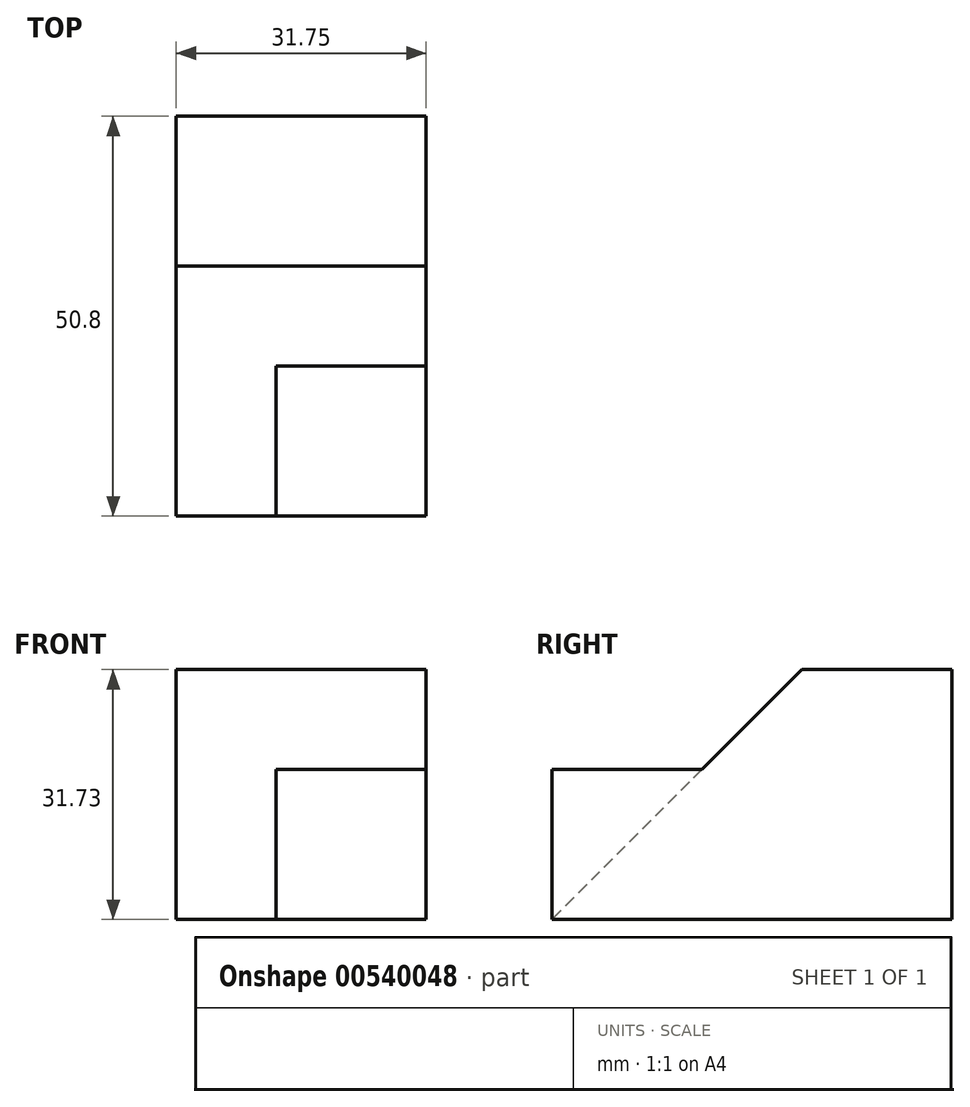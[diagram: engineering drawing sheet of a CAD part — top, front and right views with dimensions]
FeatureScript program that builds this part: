
annotation { "Feature Type Name" : "Feature", "Feature Type Description" : "" }
export const myFeature = defineFeature(function(context is Context, id is Id, definition is map)
    precondition{}
    {
        {
            var Q0;
            Q0=qCreatedBy(makeId("Right.planeOp"),FACE);
            var sketch = newSketch(context, id + "F0", { "sketchPlane" : qUnion([Q0])});
            skLineSegment(sketch, "E0", {"start": v(56.82, 43.92) * mm, "end": v(37.77, 43.92) * mm});
            skLineSegment(sketch, "E1", {"start": v(37.77, 43.92) * mm, "end": v(25.07, 31.24) * mm});
            skLineSegment(sketch, "E2", {"start": v(25.07, 31.24) * mm, "end": v(6.02, 31.24) * mm});
            skLineSegment(sketch, "E3", {"start": v(6.02, 31.24) * mm, "end": v(6.02, 12.2) * mm});
            skLineSegment(sketch, "E4", {"start": v(6.02, 12.2) * mm, "end": v(56.82, 12.2) * mm});
            skLineSegment(sketch, "E5", {"start": v(25.07, 31.24) * mm, "end": v(6.02, 12.2) * mm});
            skLineSegment(sketch, "E6", {"start": v(56.82, 43.92) * mm, "end": v(56.82, 12.2) * mm});
            skSolve(sketch);
        }
        {
            var Q0;
            Q0=makeQuery(id+"F0.imprint","IMPRINT",FACE,{"disambiguationData":[TD([[makeQuery(id+"F0.imprint","IMPRINT",EDGE,{"derivedFrom":sQuery(id+"F0.wireOp",EDGE,"E2")}),1.0]])]});
            extrude(context, id + "F1", {"entities" : qUnion([Q0]), "depth" : 31.75 * mm, "offsetDistance" : 25.4 * mm});
        }
        {
            var Q0;
            Q0 = qSketchRegion(id + "F0", true);
            extrude(context, id + "F2", {"entities" : qUnion([Q0]), "operationType" : NewBodyOperationType.ADD, "depth" : 31.75 * mm, "offsetDistance" : 25.4 * mm});
        }
        {
            var Q0;
            {var subQ0=sQuery(id+"F0.wireOp",EDGE,"E3");var subQ1=sQuery(id+"F0.wireOp",EDGE,"E2");Q0=makeQuery(id+"F2.boolean.opBoolean","MERGE",FACE,{"derivedFrom":[makeQuery(id+"F1.opExtrude","CAP_FACE",FACE,{"disambiguationData":[OSD([subQ1,subQ0,sQuery(id+"F0.wireOp",EDGE,"E5")])],"isStart":true}),makeQuery(id+"F2.opExtrude","CAP_FACE",FACE,{"disambiguationData":[OSD([sQuery(id+"F0.wireOp",EDGE,"E0"),sQuery(id+"F0.wireOp",EDGE,"E1"),subQ1,subQ0,sQuery(id+"F0.wireOp",EDGE,"E4"),sQuery(id+"F0.wireOp",EDGE,"E6")])],"isStart":true})]});}
            var sketch = newSketch(context, id + "F3", { "sketchPlane" : qUnion([Q0])});
            skLineSegment(sketch, "E7", {"start": v(-25.07, 31.24) * mm, "end": v(-6.02, 12.2) * mm});
            skSolve(sketch);
        }
        {
            var Q0;
            Q0=makeQuery(id+"F3.imprint","IMPRINT",FACE,{"disambiguationData":[TD([[makeQuery(id+"F3.imprint","IMPRINT",EDGE,{"derivedFrom":sQuery(id+"F3.wireOp",EDGE,"E7")}),1.0]])]});
            extrude(context, id + "F4", {"entities" : qUnion([Q0]), "operationType" : NewBodyOperationType.REMOVE, "oppositeDirection" : true, "depth" : 12.7 * mm, "offsetDistance" : 25.4 * mm});
        }
    });
